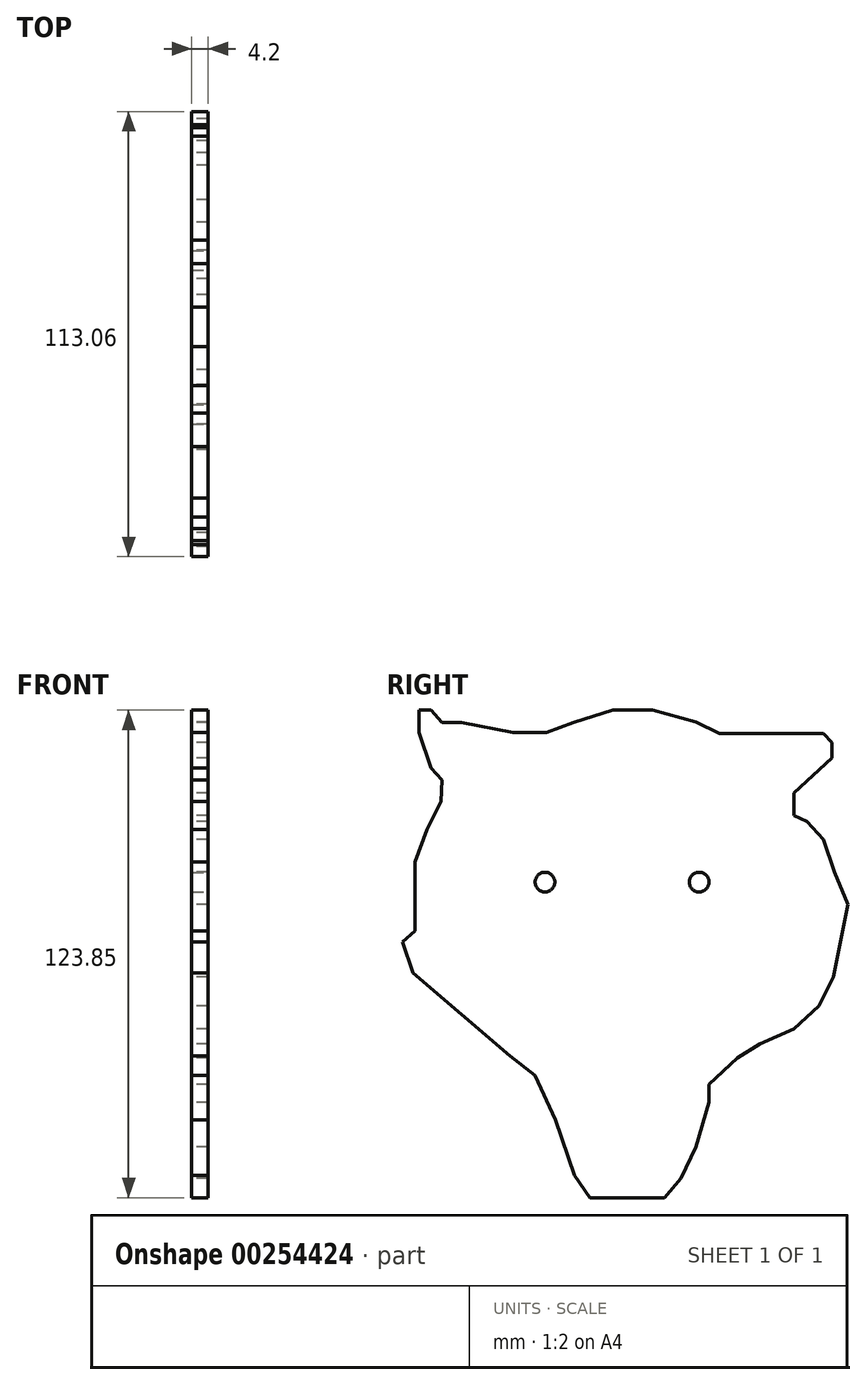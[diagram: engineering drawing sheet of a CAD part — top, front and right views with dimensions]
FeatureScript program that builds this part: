
annotation { "Feature Type Name" : "Feature", "Feature Type Description" : "" }
export const myFeature = defineFeature(function(context is Context, id is Id, definition is map)
    precondition{}
    {
        {
            var Q0;
            Q0=qCreatedBy(makeId("Right.planeOp"),FACE);
            var sketch = newSketch(context, id + "F0", { "sketchPlane" : qUnion([Q0])});
            skLineSegment(sketch, "E0", {"start": v(-46.93, 38.92) * mm, "end": v(-50.53, 31.73) * mm});
            skLineSegment(sketch, "E1", {"start": v(-50.53, 31.73) * mm, "end": v(-53.6, 23.5) * mm});
            skLineSegment(sketch, "E2", {"start": v(-53.6, 23.5) * mm, "end": v(-53.6, 17.6) * mm});
            skLineSegment(sketch, "E3", {"start": v(-53.6, 17.6) * mm, "end": v(-53.6, 10.66) * mm});
            skLineSegment(sketch, "E4", {"start": v(-53.6, 10.66) * mm, "end": v(-53.6, 6.03) * mm});
            skLineSegment(sketch, "E5", {"start": v(-53.6, 6.03) * mm, "end": v(-56.7, 3.2) * mm});
            skLineSegment(sketch, "E6", {"start": v(-56.7, 3.2) * mm, "end": v(-54.12, -4.76) * mm});
            skLineSegment(sketch, "E7", {"start": v(-54.12, -4.76) * mm, "end": v(-29.45, -25.83) * mm});
            skLineSegment(sketch, "E8", {"start": v(-29.45, -25.83) * mm, "end": v(-23.03, -30.71) * mm});
            skLineSegment(sketch, "E9", {"start": v(-23.03, -30.71) * mm, "end": v(-17.9, -42.02) * mm});
            skLineSegment(sketch, "E10", {"start": v(-17.9, -42.02) * mm, "end": v(-13, -56.15) * mm});
            skLineSegment(sketch, "E11", {"start": v(-13, -56.15) * mm, "end": v(-9.15, -61.8) * mm});
            skLineSegment(sketch, "E12", {"start": v(-9.15, -61.8) * mm, "end": v(-3.24, -61.8) * mm});
            skLineSegment(sketch, "E13", {"start": v(-3.24, -61.8) * mm, "end": v(3.7, -61.8) * mm});
            skLineSegment(sketch, "E14", {"start": v(3.7, -61.8) * mm, "end": v(9.86, -61.8) * mm});
            skLineSegment(sketch, "E15", {"start": v(9.86, -61.8) * mm, "end": v(13.97, -56.92) * mm});
            skLineSegment(sketch, "E16", {"start": v(13.97, -56.92) * mm, "end": v(17.83, -48.96) * mm});
            skLineSegment(sketch, "E17", {"start": v(17.83, -48.96) * mm, "end": v(21.17, -37.65) * mm});
            skLineSegment(sketch, "E18", {"start": v(21.17, -37.65) * mm, "end": v(21.17, -33.03) * mm});
            skLineSegment(sketch, "E19", {"start": v(21.17, -33.03) * mm, "end": v(28.36, -26.34) * mm});
            skLineSegment(sketch, "E20", {"start": v(28.36, -26.34) * mm, "end": v(34.01, -22.75) * mm});
            skLineSegment(sketch, "E21", {"start": v(34.01, -22.75) * mm, "end": v(42.75, -18.9) * mm});
            skLineSegment(sketch, "E22", {"start": v(42.75, -18.9) * mm, "end": v(49, -13.08) * mm});
            skLineSegment(sketch, "E23", {"start": v(49, -13.08) * mm, "end": v(52.68, -5.74) * mm});
            skLineSegment(sketch, "E24", {"start": v(52.68, -5.74) * mm, "end": v(54.57, 3.2) * mm});
            skLineSegment(sketch, "E25", {"start": v(54.57, 3.2) * mm, "end": v(56.37, 12.71) * mm});
            skLineSegment(sketch, "E26", {"start": v(56.37, 12.71) * mm, "end": v(53.03, 20.94) * mm});
            skLineSegment(sketch, "E27", {"start": v(53.03, 20.94) * mm, "end": v(50.2, 29.16) * mm});
            skLineSegment(sketch, "E28", {"start": v(50.2, 29.16) * mm, "end": v(45.96, 33.73) * mm});
            skLineSegment(sketch, "E29", {"start": v(45.96, 33.73) * mm, "end": v(42.75, 35.33) * mm});
            skLineSegment(sketch, "E30", {"start": v(42.75, 35.33) * mm, "end": v(42.75, 38.4) * mm});
            skLineSegment(sketch, "E31", {"start": v(42.75, 38.4) * mm, "end": v(42.75, 40.98) * mm});
            skLineSegment(sketch, "E32", {"start": v(42.75, 40.98) * mm, "end": v(46.92, 44.85) * mm});
            skLineSegment(sketch, "E33", {"start": v(46.92, 44.85) * mm, "end": v(52.35, 49.9) * mm});
            skLineSegment(sketch, "E34", {"start": v(52.35, 49.9) * mm, "end": v(52.35, 53.83) * mm});
            skLineSegment(sketch, "E35", {"start": v(52.35, 53.83) * mm, "end": v(50.2, 56.14) * mm});
            skLineSegment(sketch, "E36", {"start": v(50.2, 56.14) * mm, "end": v(42.75, 56.14) * mm});
            skLineSegment(sketch, "E37", {"start": v(42.75, 56.14) * mm, "end": v(32.22, 56.14) * mm});
            skLineSegment(sketch, "E38", {"start": v(32.22, 56.14) * mm, "end": v(23.74, 56.14) * mm});
            skLineSegment(sketch, "E39", {"start": v(23.74, 56.14) * mm, "end": v(17.83, 59.1) * mm});
            skLineSegment(sketch, "E40", {"start": v(17.83, 59.1) * mm, "end": v(6.78, 62.05) * mm});
            skLineSegment(sketch, "E41", {"start": v(6.78, 62.05) * mm, "end": v(3.7, 62.05) * mm});
            skLineSegment(sketch, "E42", {"start": v(3.7, 62.05) * mm, "end": v(-3.24, 62.05) * mm});
            skLineSegment(sketch, "E43", {"start": v(-3.24, 62.05) * mm, "end": v(-13.27, 58.97) * mm});
            skLineSegment(sketch, "E44", {"start": v(-13.27, 58.97) * mm, "end": v(-20.2, 56.4) * mm});
            skLineSegment(sketch, "E45", {"start": v(-20.2, 56.4) * mm, "end": v(-28.68, 56.4) * mm});
            skLineSegment(sketch, "E46", {"start": v(-28.68, 56.4) * mm, "end": v(-41.79, 58.97) * mm});
            skLineSegment(sketch, "E47", {"start": v(-41.79, 58.97) * mm, "end": v(-46.67, 58.97) * mm});
            skLineSegment(sketch, "E48", {"start": v(-46.67, 58.97) * mm, "end": v(-49.53, 62.05) * mm});
            skLineSegment(sketch, "E49", {"start": v(-49.53, 62.05) * mm, "end": v(-52.58, 62.05) * mm});
            skLineSegment(sketch, "E50", {"start": v(-52.58, 62.05) * mm, "end": v(-52.58, 56.4) * mm});
            skLineSegment(sketch, "E51", {"start": v(-52.58, 56.4) * mm, "end": v(-49.53, 47.4) * mm});
            skLineSegment(sketch, "E52", {"start": v(-49.53, 47.4) * mm, "end": v(-46.67, 44.32) * mm});
            skLineSegment(sketch, "E53", {"start": v(-46.67, 44.32) * mm, "end": v(-46.93, 38.92) * mm});
            skSolve(sketch);
        }
        {
            var Q0;
            Q0=makeQuery(id+"F0.imprint","IMPRINT",FACE,{"disambiguationData":[TD([[makeQuery(id+"F0.imprint","IMPRINT",EDGE,{"derivedFrom":sQuery(id+"F0.wireOp",EDGE,"E0")}),1.0]])]});
            extrude(context, id + "F1", {"entities" : qUnion([Q0]), "depth" : 4.2 * mm});
        }
        {
            var Q0;
            Q0=makeQuery(id+"F1.opExtrude","CAP_FACE",FACE,{"disambiguationData":[OSD([sQuery(id+"F0.wireOp",EDGE,"E0"),sQuery(id+"F0.wireOp",EDGE,"E1"),sQuery(id+"F0.wireOp",EDGE,"E2"),sQuery(id+"F0.wireOp",EDGE,"E3"),sQuery(id+"F0.wireOp",EDGE,"E4"),sQuery(id+"F0.wireOp",EDGE,"E5"),sQuery(id+"F0.wireOp",EDGE,"E6"),sQuery(id+"F0.wireOp",EDGE,"E7"),sQuery(id+"F0.wireOp",EDGE,"E8"),sQuery(id+"F0.wireOp",EDGE,"E9"),sQuery(id+"F0.wireOp",EDGE,"E10"),sQuery(id+"F0.wireOp",EDGE,"E11"),sQuery(id+"F0.wireOp",EDGE,"E12"),sQuery(id+"F0.wireOp",EDGE,"E13"),sQuery(id+"F0.wireOp",EDGE,"E14"),sQuery(id+"F0.wireOp",EDGE,"E15"),sQuery(id+"F0.wireOp",EDGE,"E16"),sQuery(id+"F0.wireOp",EDGE,"E17"),sQuery(id+"F0.wireOp",EDGE,"E18"),sQuery(id+"F0.wireOp",EDGE,"E19"),sQuery(id+"F0.wireOp",EDGE,"E20"),sQuery(id+"F0.wireOp",EDGE,"E21"),sQuery(id+"F0.wireOp",EDGE,"E22"),sQuery(id+"F0.wireOp",EDGE,"E23"),sQuery(id+"F0.wireOp",EDGE,"E24"),sQuery(id+"F0.wireOp",EDGE,"E25"),sQuery(id+"F0.wireOp",EDGE,"E26"),sQuery(id+"F0.wireOp",EDGE,"E27"),sQuery(id+"F0.wireOp",EDGE,"E28"),sQuery(id+"F0.wireOp",EDGE,"E29"),sQuery(id+"F0.wireOp",EDGE,"E30"),sQuery(id+"F0.wireOp",EDGE,"E31"),sQuery(id+"F0.wireOp",EDGE,"E32"),sQuery(id+"F0.wireOp",EDGE,"E33"),sQuery(id+"F0.wireOp",EDGE,"E34"),sQuery(id+"F0.wireOp",EDGE,"E35"),sQuery(id+"F0.wireOp",EDGE,"E36"),sQuery(id+"F0.wireOp",EDGE,"E37"),sQuery(id+"F0.wireOp",EDGE,"E38"),sQuery(id+"F0.wireOp",EDGE,"E39"),sQuery(id+"F0.wireOp",EDGE,"E40"),sQuery(id+"F0.wireOp",EDGE,"E41"),sQuery(id+"F0.wireOp",EDGE,"E42"),sQuery(id+"F0.wireOp",EDGE,"E43"),sQuery(id+"F0.wireOp",EDGE,"E44"),sQuery(id+"F0.wireOp",EDGE,"E45"),sQuery(id+"F0.wireOp",EDGE,"E46"),sQuery(id+"F0.wireOp",EDGE,"E47"),sQuery(id+"F0.wireOp",EDGE,"E48"),sQuery(id+"F0.wireOp",EDGE,"E49"),sQuery(id+"F0.wireOp",EDGE,"E50"),sQuery(id+"F0.wireOp",EDGE,"E51"),sQuery(id+"F0.wireOp",EDGE,"E52"),sQuery(id+"F0.wireOp",EDGE,"E53")])],"isStart":false});
            var sketch = newSketch(context, id + "F2", { "sketchPlane" : qUnion([Q0])});
            skPoint(sketch, "E54", {"position": v(-20.55, 18.38) * mm});
            skPoint(sketch, "E55", {"position": v(18.62, 18.38) * mm});
            skSolve(sketch);
        }
        {
            var Q0;
            Q0=sQuery(id+"F2.wireOp",VERTEX,"E54");
            var Q1;
            Q1=sQuery(id+"F2.wireOp",VERTEX,"E55");
            var Q2;
            Q2=makeQuery(id+"F1.opExtrude","SWEPT_BODY",BODY,{"disambiguationData":[OSD([sQuery(id+"F0.wireOp",EDGE,"E0"),sQuery(id+"F0.wireOp",EDGE,"E1"),sQuery(id+"F0.wireOp",EDGE,"E2"),sQuery(id+"F0.wireOp",EDGE,"E3"),sQuery(id+"F0.wireOp",EDGE,"E4"),sQuery(id+"F0.wireOp",EDGE,"E5"),sQuery(id+"F0.wireOp",EDGE,"E6"),sQuery(id+"F0.wireOp",EDGE,"E7"),sQuery(id+"F0.wireOp",EDGE,"E8"),sQuery(id+"F0.wireOp",EDGE,"E9"),sQuery(id+"F0.wireOp",EDGE,"E10"),sQuery(id+"F0.wireOp",EDGE,"E11"),sQuery(id+"F0.wireOp",EDGE,"E12"),sQuery(id+"F0.wireOp",EDGE,"E13"),sQuery(id+"F0.wireOp",EDGE,"E14"),sQuery(id+"F0.wireOp",EDGE,"E15"),sQuery(id+"F0.wireOp",EDGE,"E16"),sQuery(id+"F0.wireOp",EDGE,"E17"),sQuery(id+"F0.wireOp",EDGE,"E18"),sQuery(id+"F0.wireOp",EDGE,"E19"),sQuery(id+"F0.wireOp",EDGE,"E20"),sQuery(id+"F0.wireOp",EDGE,"E21"),sQuery(id+"F0.wireOp",EDGE,"E22"),sQuery(id+"F0.wireOp",EDGE,"E23"),sQuery(id+"F0.wireOp",EDGE,"E24"),sQuery(id+"F0.wireOp",EDGE,"E25"),sQuery(id+"F0.wireOp",EDGE,"E26"),sQuery(id+"F0.wireOp",EDGE,"E27"),sQuery(id+"F0.wireOp",EDGE,"E28"),sQuery(id+"F0.wireOp",EDGE,"E29"),sQuery(id+"F0.wireOp",EDGE,"E30"),sQuery(id+"F0.wireOp",EDGE,"E31"),sQuery(id+"F0.wireOp",EDGE,"E32"),sQuery(id+"F0.wireOp",EDGE,"E33"),sQuery(id+"F0.wireOp",EDGE,"E34"),sQuery(id+"F0.wireOp",EDGE,"E35"),sQuery(id+"F0.wireOp",EDGE,"E36"),sQuery(id+"F0.wireOp",EDGE,"E37"),sQuery(id+"F0.wireOp",EDGE,"E38"),sQuery(id+"F0.wireOp",EDGE,"E39"),sQuery(id+"F0.wireOp",EDGE,"E40"),sQuery(id+"F0.wireOp",EDGE,"E41"),sQuery(id+"F0.wireOp",EDGE,"E42"),sQuery(id+"F0.wireOp",EDGE,"E43"),sQuery(id+"F0.wireOp",EDGE,"E44"),sQuery(id+"F0.wireOp",EDGE,"E45"),sQuery(id+"F0.wireOp",EDGE,"E46"),sQuery(id+"F0.wireOp",EDGE,"E47"),sQuery(id+"F0.wireOp",EDGE,"E48"),sQuery(id+"F0.wireOp",EDGE,"E49"),sQuery(id+"F0.wireOp",EDGE,"E50"),sQuery(id+"F0.wireOp",EDGE,"E51"),sQuery(id+"F0.wireOp",EDGE,"E52"),sQuery(id+"F0.wireOp",EDGE,"E53")])]});
            hole(context, id + "F3", {"style" : HoleStyle.SIMPLE, "endStyle" : HoleEndStyle.BLIND, "holeDiameter" : 5 * mm, "holeDepth" : 12 * mm, "tappedDepth" : 12 * mm, "tapClearance" : 3, "locations" : qUnion([Q0, Q1]), "scope" : qUnion([Q2])});
        }
    });
